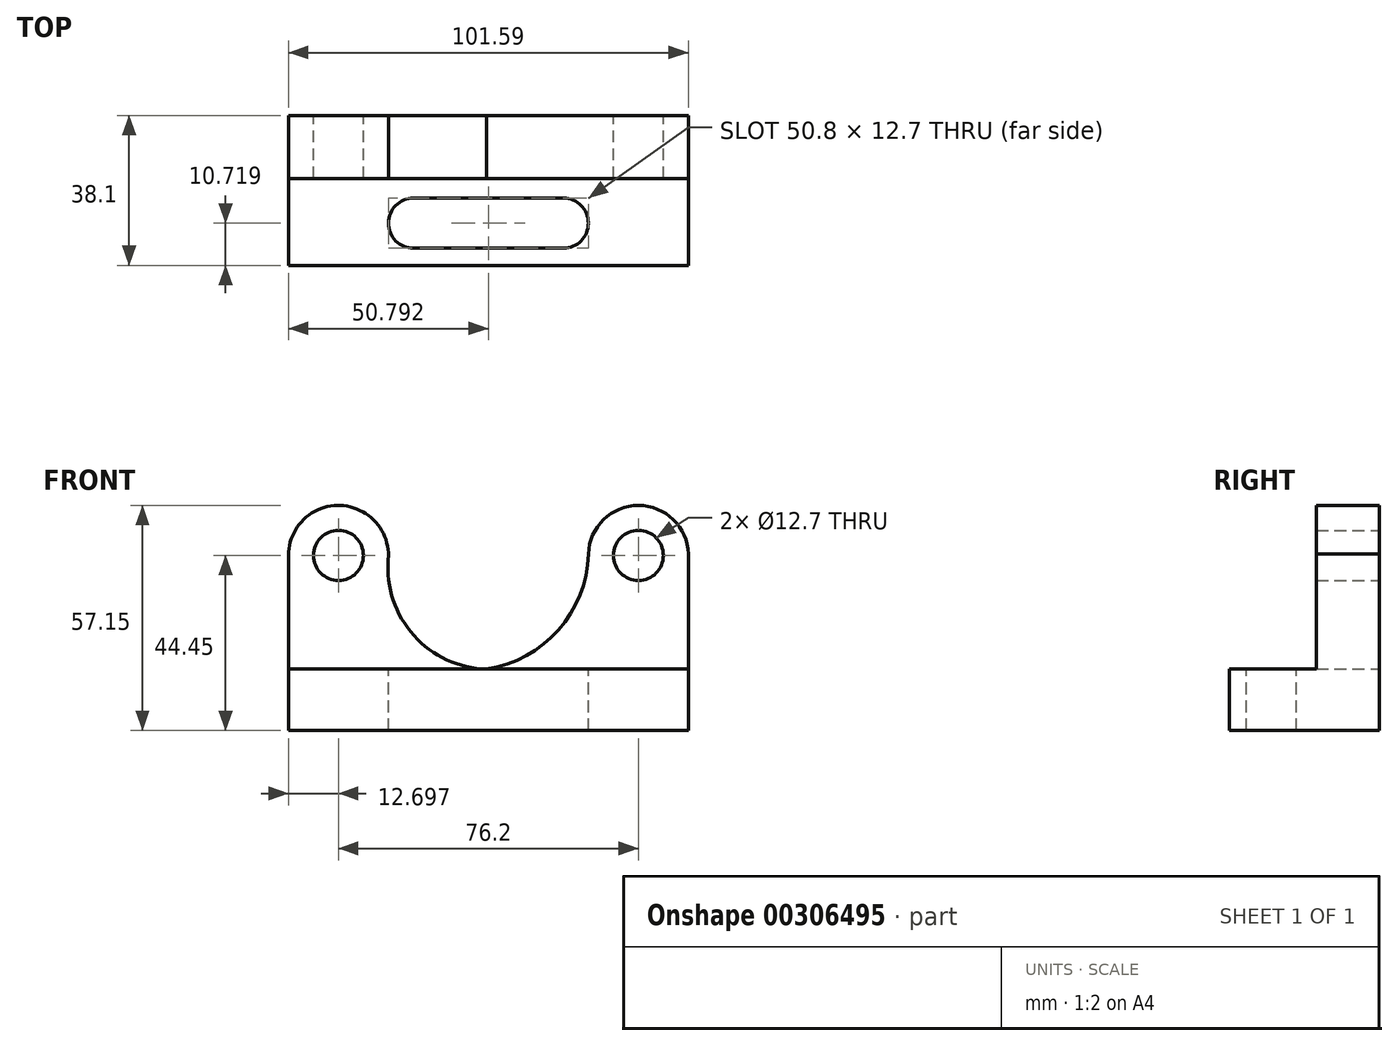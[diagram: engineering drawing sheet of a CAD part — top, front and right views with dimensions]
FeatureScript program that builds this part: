
annotation { "Feature Type Name" : "Feature", "Feature Type Description" : "" }
export const myFeature = defineFeature(function(context is Context, id is Id, definition is map)
    precondition{}
    {
        {
            var Q0;
            Q0=qCreatedBy(makeId("Front.planeOp"),FACE);
            var sketch = newSketch(context, id + "F0", { "sketchPlane" : qUnion([Q0])});
            skLineSegment(sketch, "E0", {"start": v(-109.88, 0) * mm, "end": v(-8.29, 0) * mm});
            skLineSegment(sketch, "E1", {"start": v(-109.88, 0) * mm, "end": v(-109.88, 44.45) * mm});
            skLineSegment(sketch, "E2", {"start": v(-8.29, 0) * mm, "end": v(-8.29, 44.82) * mm});
            skArc(sketch, "E3", {"start": v(-84.52, 43.42) * mm, "mid": v(-96.67, 57.14) * mm, "end": v(-109.88, 44.45) * mm});
            skArc(sketch, "E4", {"start": v(-8.29, 44.82) * mm, "mid": v(-20.98, 57.15) * mm, "end": v(-33.68, 44.82) * mm});
            skCircle(sketch, "E5", {"center": v(-97.18, 44.45) * mm, "radius": 6.35 * mm});
            skCircle(sketch, "E6", {"center": v(-20.98, 44.45) * mm, "radius": 6.35 * mm});
            skLineSegment(sketch, "E7", {"start": v(-109.88, 15.56) * mm, "end": v(-8.29, 15.56) * mm});
            skArc(sketch, "E8", {"start": v(-33.68, 44.82) * mm, "mid": v(-41.31, 25.5) * mm, "end": v(-59.54, 15.56) * mm});
            skArc(sketch, "E9", {"start": v(-84.52, 43.42) * mm, "mid": v(-78.03, 24.12) * mm, "end": v(-59.54, 15.56) * mm});
            skSolve(sketch);
        }
        {
            var Q0;
            {var subQ1=sQuery(id+"F0.wireOp",EDGE,"E3");Q0=makeQuery(id+"F0.imprint","IMPRINT",FACE,{"disambiguationData":[TD([[makeQuery(id+"F0.imprint","IMPRINT",EDGE,{"derivedFrom":subQ1}),1.0]])]});}
            var Q1;
            {var subQ4=sQuery(id+"F0.wireOp",EDGE,"E4");Q1=makeQuery(id+"F0.imprint","IMPRINT",FACE,{"disambiguationData":[TD([[makeQuery(id+"F0.imprint","IMPRINT",EDGE,{"derivedFrom":subQ4}),1.0]])]});}
            extrude(context, id + "F1", {"entities" : qUnion([Q0, Q1]), "depth" : 16 * mm});
        }
        {
            var Q0;
            {var subQ0=sQuery(id+"F0.wireOp",EDGE,"E0");Q0=makeQuery(id+"F0.imprint","IMPRINT",FACE,{"disambiguationData":[TD([[makeQuery(id+"F0.imprint","IMPRINT",EDGE,{"derivedFrom":subQ0}),1.0]])]});}
            extrude(context, id + "F2", {"entities" : qUnion([Q0]), "operationType" : NewBodyOperationType.ADD, "depth" : 38.1 * mm});
        }
        {
            var Q0;
            Q0=makeQuery(id+"F2.opExtrude","SWEPT_FACE",FACE,{"disambiguationData":[OSD([sQuery(id+"F0.wireOp",EDGE,"E7")])]});
            var sketch = newSketch(context, id + "F3", { "sketchPlane" : qUnion([Q0])});
            skLineSegment(sketch, "E10", {"start": v(-109.88, -16) * mm, "end": v(-8.29, -16) * mm});
            skArc(sketch, "E11", {"start": v(-78.14, -21.03) * mm, "mid": v(-84.49, -27.38) * mm, "end": v(-78.14, -33.73) * mm});
            skArc(sketch, "E12", {"start": v(-40.04, -21.03) * mm, "mid": v(-33.69, -27.38) * mm, "end": v(-40.04, -33.73) * mm});
            skLineSegment(sketch, "E13", {"start": v(-78.14, -21.03) * mm, "end": v(-40.04, -21.03) * mm});
            skLineSegment(sketch, "E14", {"start": v(-78.14, -33.73) * mm, "end": v(-40.04, -33.73) * mm});
            skSolve(sketch);
        }
        {
            var Q0;
            Q0 = qSketchRegion(id + "F3", true);
            extrude(context, id + "F4", {"entities" : qUnion([Q0]), "operationType" : NewBodyOperationType.REMOVE, "oppositeDirection" : true, "depth" : 25.4 * mm});
        }
    });
